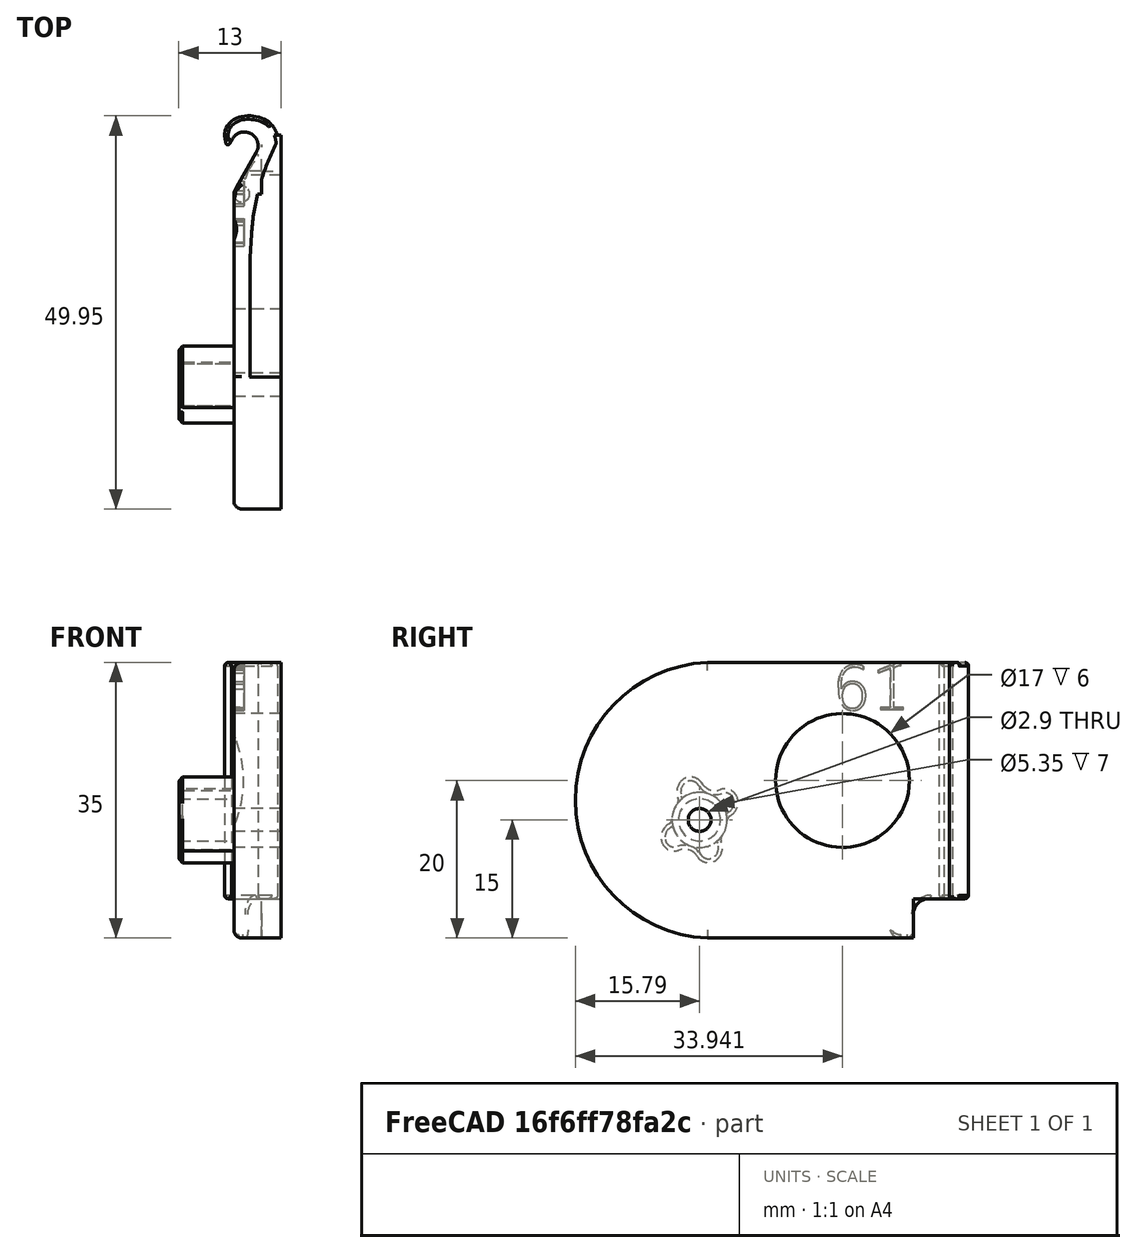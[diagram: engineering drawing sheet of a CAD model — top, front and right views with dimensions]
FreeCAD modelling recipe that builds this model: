
FCSTD DOCUMENT  (FreeCAD 0.18R)
Label: hinge-right-161deg-flat
License: All rights reserved
LicenseURL: http://en.wikipedia.org/wiki/All_rights_reserved
objects: App::FeaturePython×4, Part::FeaturePython×2, Part::Part2DObjectPython×1, Part::Extrusion×1, Part::Cut×1
note: 5 computed .brp shape members not serialized (recipe doc carries the construction recipe); baked Part::Feature solids carry a one-line shape summary decoded from their .brp

FEATURE [Part::FeaturePython] pillar_base_001  label="pillar-base_001"  # a2plus imported part (geometry in sourceFile) (typed FeaturePython)
  Placement = pos=(0.000608724,-57.4623,23.2104) rot=(-1,0,0;0.76777rad)
  a2p_Version = V0.1
  fixedPosition = false
  objectType = a2pPart
  sourceFile = ./parts/pillar-base.fcstd
  subassemblyImport = false
  timeLastImport = 1.60452e+09
  updateColors = true
FEATURE [Part::Part2DObjectPython] ShapeString  # Draft 2D object (typed FeaturePython)
  FontFile = <path>
  Placement = pos=(1.61,10.5,29) rot=(0.57735,-0.57735,-0.57735;2.0944rad)
  Size = 6
  String = 61
  Tracking = 0
FEATURE [Part::Extrusion] Extrude
  Base = -> ShapeString
  Dir = (-1,0,0)
  DirMode = 2
  FaceMakerClass = Part::FaceMakerBullseye
  LengthFwd = 3.5
  LengthRev = 0
  Placement = pos=(0,0,0) rot=(0,0,1;3.14159rad)
  Solid = false
  Symmetric = false
FEATURE [Part::FeaturePython] bracket_right_flat_001  label="bracket-right-flat_001"  # a2plus imported part (geometry in sourceFile) (typed FeaturePython)
  Placement = pos=(0,0,0) rot=(0,0,1;3.14159rad)
  a2p_Version = V0.1
  fixedPosition = true
  objectType = a2pPart
  sourceFile = ./parts/bracket-right-flat.fcstd
  subassemblyImport = false
  timeLastImport = 1.60489e+09
  updateColors = true
FEATURE [App::FeaturePython] axisCoincident_001  label="axisCoincident_001__bracket-right-flat_001"  # a2plus constraint (typed FeaturePython)
  Object1 = pillar_base_001
  Object2 = bracket_right_flat_001
  ParentTreeObject = -> pillar_base_001
  SubElement1 = Face17
  SubElement2 = Face31
  Suppressed = false
  Type = axial
  directionConstraint = 1
  lockRotation = false
FEATURE [App::FeaturePython] axisCoincident_001_mirror  label="axisCoincident_001__pillar-base_001"  # a2plus constraint (typed FeaturePython)
  Object1 = pillar_base_001
  Object2 = bracket_right_flat_001
  ParentTreeObject = -> bracket_right_flat_001
  SubElement1 = Face17
  SubElement2 = Face31
  Suppressed = false
  Type = axial
  directionConstraint = 1
  lockRotation = false
FEATURE [App::FeaturePython] planeCoincident_001  label="planeCoincident_001__bracket-right-flat_001"  # a2plus constraint (typed FeaturePython)
  Object1 = pillar_base_001
  Object2 = bracket_right_flat_001
  ParentTreeObject = -> pillar_base_001
  SubElement1 = Face1
  SubElement2 = Face57
  Suppressed = false
  Type = plane
  directionConstraint = 1
  offset = 0
FEATURE [App::FeaturePython] planeCoincident_001_mirror  label="planeCoincident_001__pillar-base_001"  # a2plus constraint (typed FeaturePython)
  Object1 = pillar_base_001
  Object2 = bracket_right_flat_001
  ParentTreeObject = -> bracket_right_flat_001
  SubElement1 = Face1
  SubElement2 = Face57
  Suppressed = false
  Type = plane
  directionConstraint = 1
  offset = 0
FEATURE [Part::Cut] Cut
  Base = -> bracket_right_flat_001
  Tool = -> Extrude
note: 1 file-system path scrubbed to <path> (originals preserved in the JSON sidecar)
